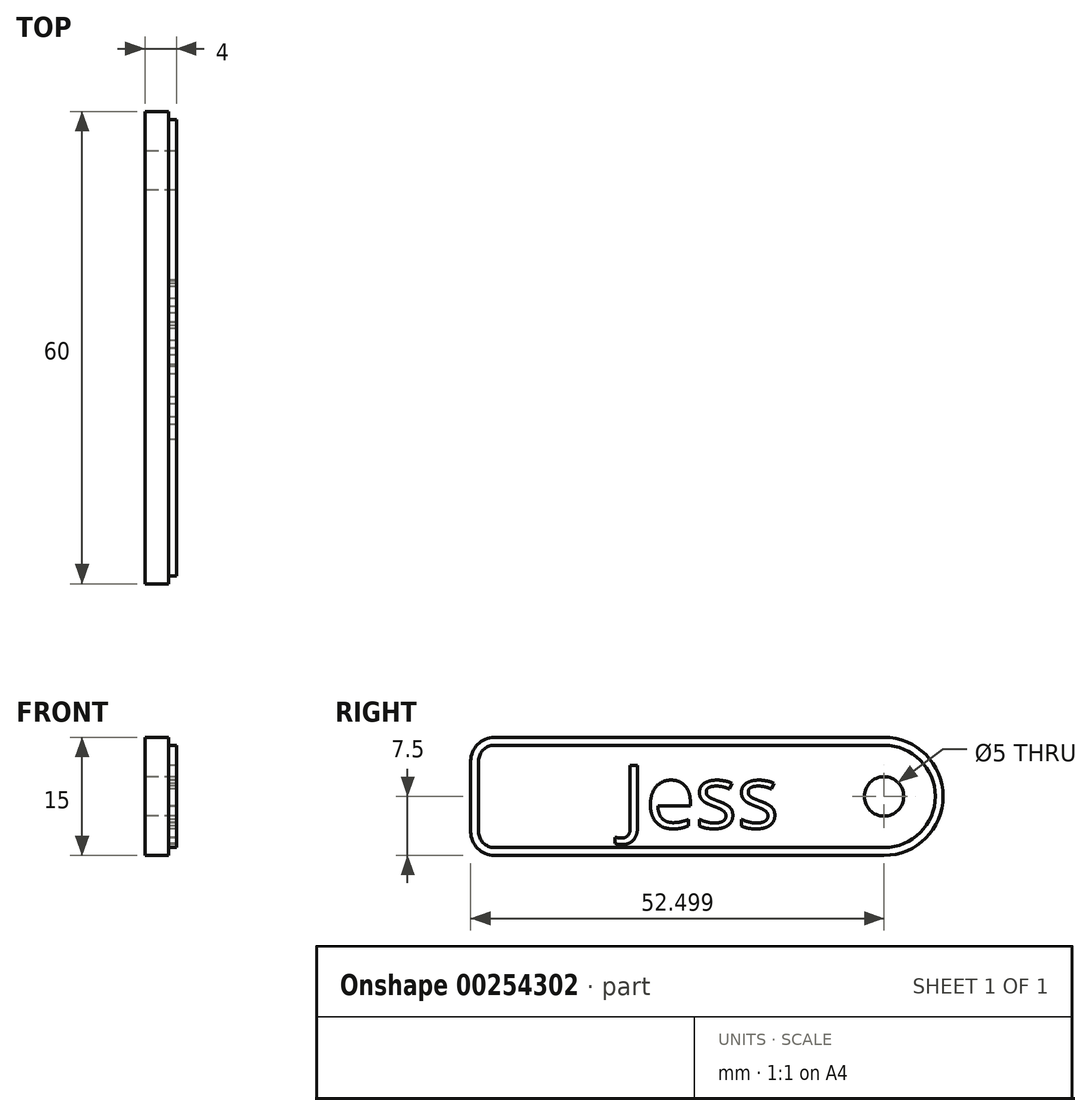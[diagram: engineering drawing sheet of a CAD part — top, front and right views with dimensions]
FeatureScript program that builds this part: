
annotation { "Feature Type Name" : "Feature", "Feature Type Description" : "" }
export const myFeature = defineFeature(function(context is Context, id is Id, definition is map)
    precondition{}
    {
        {
            var Q0;
            Q0=qCreatedBy(makeId("Right.planeOp"),FACE);
            var sketch = newSketch(context, id + "F0", { "sketchPlane" : qUnion([Q0])});
            skLineSegment(sketch, "E0.bottom", {"start": v(-26.71, 7.5) * mm, "end": v(22.79, 7.5) * mm});
            skLineSegment(sketch, "E0.top", {"start": v(-26.71, -7.5) * mm, "end": v(22.79, -7.5) * mm});
            skLineSegment(sketch, "E0.left", {"start": v(-29.71, 4.5) * mm, "end": v(-29.71, -4.5) * mm});
            skArc(sketch, "E1", {"start": v(22.79, -7.5) * mm, "mid": v(30.29, 0) * mm, "end": v(22.79, 7.5) * mm});
            skPoint(sketch, "E2.visualSharp", {"position": v(-29.71, 7.5) * mm});
            skArc(sketch, "E2.filletArc", {"start": v(-26.71, 7.5) * mm, "mid": v(-28.83, 6.62) * mm, "end": v(-29.71, 4.5) * mm});
            skPoint(sketch, "E3.visualSharp", {"position": v(-29.71, -7.5) * mm});
            skArc(sketch, "E3.filletArc", {"start": v(-29.71, -4.5) * mm, "mid": v(-28.83, -6.62) * mm, "end": v(-26.71, -7.5) * mm});
            skCircle(sketch, "E4", {"center": v(22.79, 0) * mm, "radius": 2.5 * mm});
            skSolve(sketch);
        }
        {
            var Q0;
            Q0=makeQuery(id+"F0.imprint","IMPRINT",FACE,{"disambiguationData":[TD([[makeQuery(id+"F0.imprint","IMPRINT",EDGE,{"derivedFrom":sQuery(id+"F0.wireOp",EDGE,"E0.bottom")}),-1.0]])]});
            extrude(context, id + "F1", {"entities" : qUnion([Q0]), "depth" : 3 * mm});
        }
        {
            var Q0;
            Q0=makeQuery(id+"F1.opExtrude","CAP_FACE",FACE,{"disambiguationData":[OSD([sQuery(id+"F0.wireOp",EDGE,"E0.bottom"),sQuery(id+"F0.wireOp",EDGE,"E0.top"),sQuery(id+"F0.wireOp",EDGE,"E0.left"),sQuery(id+"F0.wireOp",EDGE,"E1"),sQuery(id+"F0.wireOp",EDGE,"E2.filletArc"),sQuery(id+"F0.wireOp",EDGE,"E3.filletArc"),sQuery(id+"F0.wireOp",EDGE,"E4")])],"isStart":false});
            var sketch = newSketch(context, id + "F2", { "sketchPlane" : qUnion([Q0])});
            skText(sketch, "E5", { "text": "Jess\n", "fontName": "OpenSans-Regular.ttf"});
            skLineSegment(sketch, "E6.0", {"start": v(-26.71, 6.5) * mm, "end": v(22.79, 6.5) * mm});
            skLineSegment(sketch, "E6.1", {"start": v(-28.71, 4.5) * mm, "end": v(-28.71, -4.5) * mm});
            skLineSegment(sketch, "E6.2", {"start": v(-26.71, -6.5) * mm, "end": v(22.79, -6.5) * mm});
            skArc(sketch, "E6.3", {"start": v(22.79, -6.5) * mm, "mid": v(29.29, 0) * mm, "end": v(22.79, 6.5) * mm});
            skArc(sketch, "E7.0", {"start": v(-26.71, 6.5) * mm, "mid": v(-28.12, 5.91) * mm, "end": v(-28.71, 4.5) * mm});
            skArc(sketch, "E8.0", {"start": v(-28.71, -4.5) * mm, "mid": v(-28.12, -5.91) * mm, "end": v(-26.71, -6.5) * mm});
            const initialGuessF2  = {"E5": [-0.0105, -0.00402, 1, 0, 0.00805]};
            skSetInitialGuess(sketch, initialGuessF2);
            skSolve(sketch);
        }
        {
            var Q0;
            Q0 = qSketchRegion(id + "F4", true);
            var Q1;
            Q1=makeQuery(id+"F2.imprint","IMPRINT",FACE,{"disambiguationData":[TD([[makeQuery(id+"F2.imprint","IMPRINT",EDGE,{"derivedFrom":sQuery(id+"F2.wireOp",EDGE,"E5.sketch_text.stroke-0")}),1.0]])]});
            extrude(context, id + "F3", {"entities" : qUnion([Q0, Q1]), "operationType" : NewBodyOperationType.ADD, "depth" : 1 * mm});
        }
        {
            var Q0;
            Q0=makeQuery(id+"Fpc81VqTZJdLZiW_1.imprint","IMPRINT",FACE,{"disambiguationData":[TD([[makeQuery(id+"Fpc81VqTZJdLZiW_1.imprint","IMPRINT",EDGE,{"derivedFrom":makeQuery(id+"F3.opExtrude","CAP_EDGE",EDGE,{"disambiguationData":[OSD([sQuery(id+"F2.wireOp",EDGE,"E5.sketch_text.stroke-0")])],"isStart":false})}),1.0]])]});
            var sketch = newSketch(context, id + "F4", { "sketchPlane" : qUnion([Q0])});
            skSolve(sketch);
        }
    });
